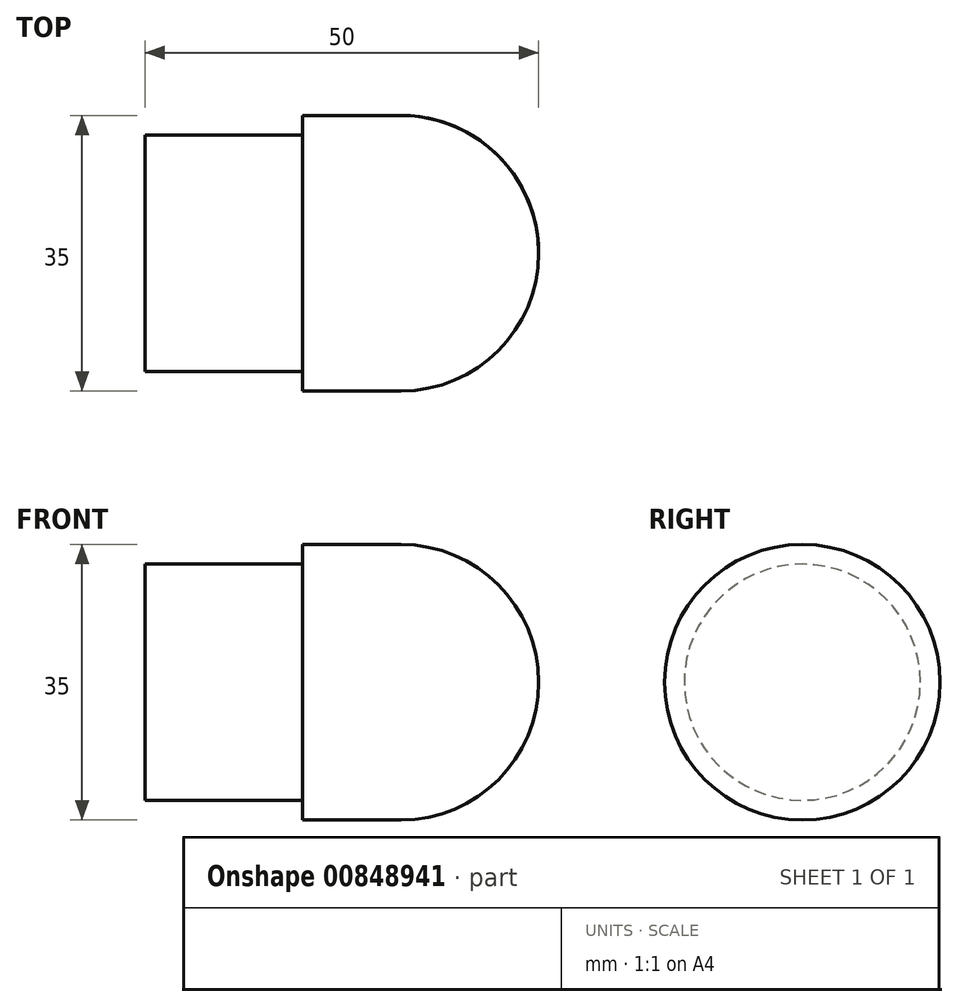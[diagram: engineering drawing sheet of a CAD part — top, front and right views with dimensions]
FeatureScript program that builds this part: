
annotation { "Feature Type Name" : "Feature", "Feature Type Description" : "" }
export const myFeature = defineFeature(function(context is Context, id is Id, definition is map)
    precondition{}
    {
        {
            var Q0;
            Q0=qCreatedBy(makeId("Top.planeOp"),FACE);
            var sketch = newSketch(context, id + "F0", { "sketchPlane" : qUnion([Q0])});
            skArc(sketch, "E0", {"start": v(17.5, 0) * mm, "mid": v(12.37, 12.37) * mm, "end": v(0, 17.5) * mm});
            skLineSegment(sketch, "E1.bottom", {"start": v(0, 0) * mm, "end": v(-12.5, 0) * mm});
            skLineSegment(sketch, "E1.top", {"start": v(0, 17.5) * mm, "end": v(-12.5, 17.5) * mm});
            skLineSegment(sketch, "E1.left", {"start": v(0, 0) * mm, "end": v(0, 17.5) * mm});
            skLineSegment(sketch, "E1.right", {"start": v(-12.5, 0) * mm, "end": v(-12.5, 17.5) * mm});
            skLineSegment(sketch, "E2.bottom", {"start": v(-12.5, 15) * mm, "end": v(-32.5, 15) * mm});
            skLineSegment(sketch, "E2.top", {"start": v(-12.5, 0) * mm, "end": v(-32.5, 0) * mm});
            skLineSegment(sketch, "E2.left", {"start": v(-12.5, 15) * mm, "end": v(-12.5, 0) * mm});
            skLineSegment(sketch, "E2.right", {"start": v(-32.5, 15) * mm, "end": v(-32.5, 0) * mm});
            skLineSegment(sketch, "E3", {"start": v(0, 0) * mm, "end": v(17.5, 0) * mm});
            skSolve(sketch);
        }
        {
            var Q0;
            Q0 = qSketchRegion(id + "F0", true);
            var Q1;
            Q1=sQuery(id+"F0.wireOp",EDGE,"E2.top");
            revolve(context, id + "F1", {"surfaceOperationType" : NewSurfaceOperationType.NEW, "entities" : qUnion([Q0]), "axis" : qUnion([Q1]), "revolveType" : RevolveType.FULL, "oppositeDirection" : true});
        }
    });
